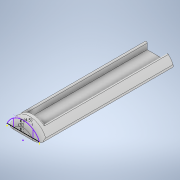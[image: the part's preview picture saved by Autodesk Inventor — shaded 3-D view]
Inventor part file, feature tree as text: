
AUTODESK INVENTOR PART (.ipt)
format: ipt  version: 2020 (Build 240168000, 168)  size: 142,336 bytes
history: native  units: in
note: dims shown in document units (in); Inventor stores cm internally (conversion verified against a paired STEP export)
features: extrude x3, sketch x2, fillet x2
ambient origin geometry x8: Origin, YZ Plane, XZ Plane, XY Plane, X Axis, Y Axis, Z Axis, Center Point
bodies: Solid1 (feature_tree)
feature tree (7):
  extrude  "Extrusion1"  Depth=0.5906in
  sketch  "Sketch2"  dims[d2=0.0394in d3=0.0in d4=0.1969in d5=0.1772in d6=0.0394in d7=0.0in d8=0.1969in d9=0.0in d10=0.0197in d11=0.1181in]
  extrude  "Extrusion2"  Depth=0.1181in
  extrude  "Extrusion3"  Depth=0.1181in
  fillet  "Fillet1"  Radius=0.0394in
  fillet  "Fillet2"  Radius=0.1969in
  sketch  "Sketch1"  dims[d0=0.5906in d1=2.4409in]
